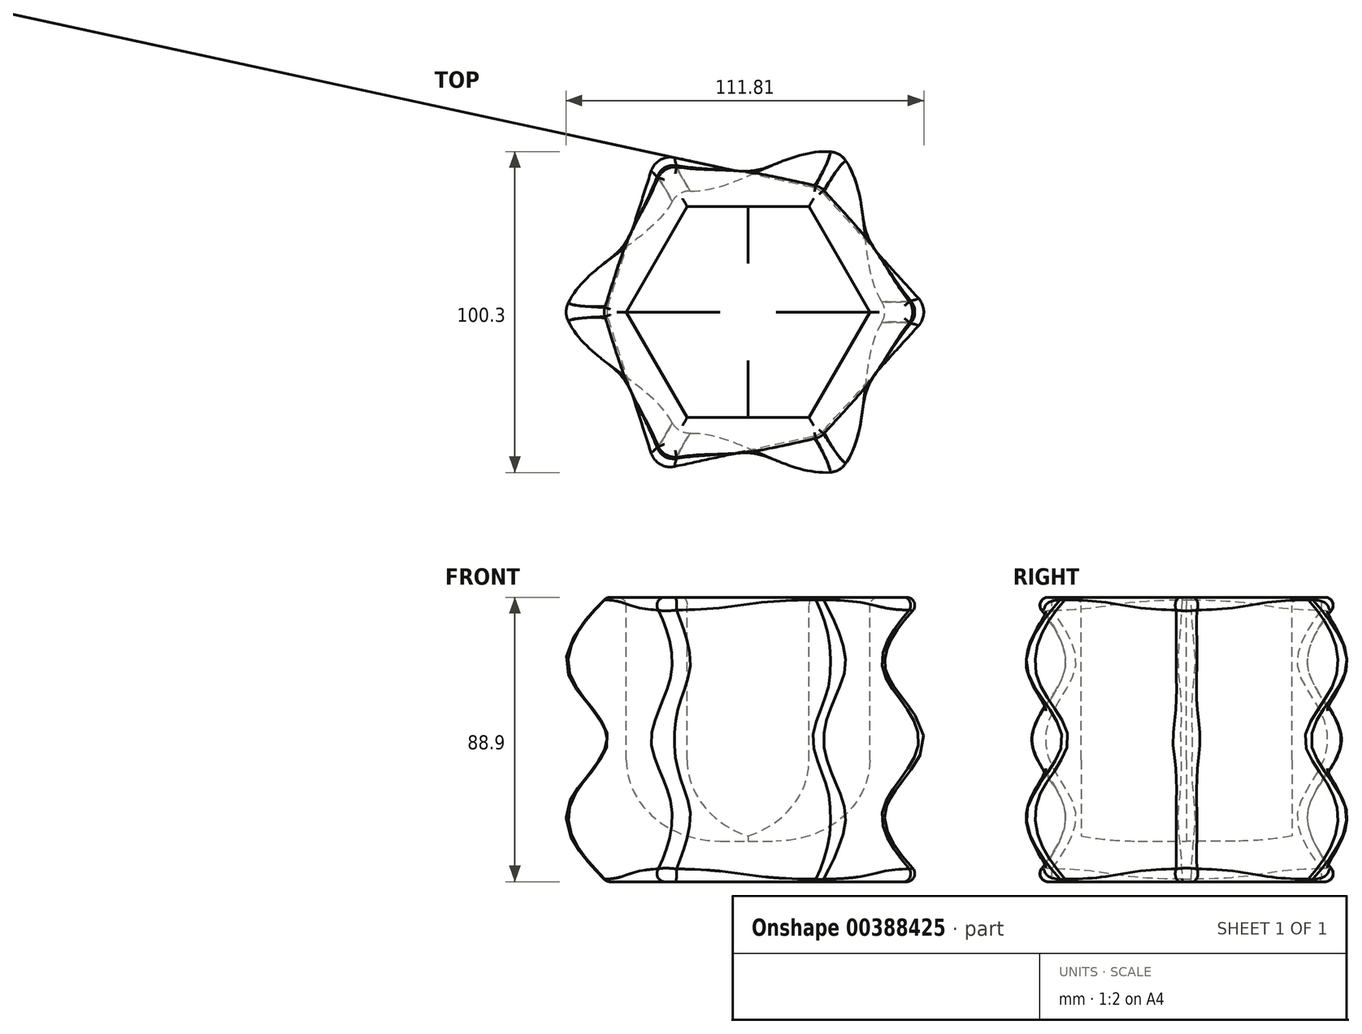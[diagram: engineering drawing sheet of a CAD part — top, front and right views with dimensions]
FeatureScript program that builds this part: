
annotation { "Feature Type Name" : "Feature", "Feature Type Description" : "" }
export const myFeature = defineFeature(function(context is Context, id is Id, definition is map)
    precondition{}
    {
        {
            var Q0;
            Q0=qCreatedBy(makeId("Top.planeOp"),FACE);
            var sketch = newSketch(context, id + "F0", { "sketchPlane" : qUnion([Q0])});
            skLineSegment(sketch, "E0.0", {"start": v(57.15, 0) * mm, "end": v(22.23, -38.5) * mm});
            skLineSegment(sketch, "E0.1", {"start": v(22.23, -38.5) * mm, "end": v(-28.58, -49.5) * mm});
            skLineSegment(sketch, "E0.2", {"start": v(-28.58, -49.5) * mm, "end": v(-44.45, 0) * mm});
            skLineSegment(sketch, "E0.3", {"start": v(-44.45, 0) * mm, "end": v(-28.58, 49.5) * mm});
            skLineSegment(sketch, "E0.4", {"start": v(-28.58, 49.5) * mm, "end": v(22.22, 38.5) * mm});
            skLineSegment(sketch, "E0.5", {"start": v(22.22, 38.5) * mm, "end": v(57.15, 0) * mm});
            skLineSegment(sketch, "E1", {"start": v(0, 0) * mm, "end": v(22.22, 38.5) * mm, "construction": true});
            skLineSegment(sketch, "E2", {"start": v(0, 0) * mm, "end": v(57.15, 0) * mm, "construction": true});
            skLineSegment(sketch, "E3", {"start": v(0, 0) * mm, "end": v(22.23, -38.5) * mm, "construction": true});
            skLineSegment(sketch, "E4", {"start": v(0, 0) * mm, "end": v(-28.58, -49.5) * mm, "construction": true});
            skLineSegment(sketch, "E5", {"start": v(0, 0) * mm, "end": v(-44.45, 0) * mm, "construction": true});
            skLineSegment(sketch, "E6", {"start": v(0, 0) * mm, "end": v(-28.58, 49.5) * mm, "construction": true});
            skSolve(sketch);
        }
        {
            var Q0;
            Q0=qCreatedBy(makeId("Top.planeOp"),FACE);
            cPlane(context, id + "F1", {"entities" : qUnion([Q0]), "cplaneType" : CPlaneType.OFFSET, "offset" : 88.9 * mm, "width" : 152.4 * mm, "height" : 152.4 * mm});
        }
        {
            var Q0;
            Q0=qCreatedBy(id+"F1.planeOp",FACE);
            var sketch = newSketch(context, id + "F2", { "sketchPlane" : qUnion([Q0])});
            skLineSegment(sketch, "E7.0.0", {"start": v(57.15, 0) * mm, "end": v(22.22, 38.5) * mm});
            skLineSegment(sketch, "E7.0.1", {"start": v(22.22, 38.5) * mm, "end": v(-28.58, 49.5) * mm});
            skLineSegment(sketch, "E7.0.2", {"start": v(-28.58, 49.5) * mm, "end": v(-44.45, 0) * mm});
            skLineSegment(sketch, "E7.0.3", {"start": v(-44.45, 0) * mm, "end": v(-28.58, -49.5) * mm});
            skLineSegment(sketch, "E7.0.4", {"start": v(-28.58, -49.5) * mm, "end": v(22.23, -38.5) * mm});
            skLineSegment(sketch, "E7.0.5", {"start": v(22.23, -38.5) * mm, "end": v(57.15, 0) * mm});
            skSolve(sketch);
        }
        {
            var Q0;
            Q0=sQuery(id+"F2.wireOp",VERTEX,"E7.0.3.start");
            var Q1;
            Q1=sQuery(id+"F2.wireOp",VERTEX,"E7.0.0.start");
            var Q2;
            Q2=sQuery(id+"F0.wireOp",VERTEX,"E0.5.end");
            cPlane(context, id + "F3", {"entities" : qUnion([Q0, Q1, Q2]), "cplaneType" : CPlaneType.THREE_POINT, "offset" : 25.4 * mm, "width" : 152.4 * mm, "height" : 152.4 * mm});
        }
        {
            var Q0;
            Q0=sQuery(id+"F2.wireOp",VERTEX,"E7.0.1.end");
            var Q1;
            Q1=sQuery(id+"F2.wireOp",VERTEX,"E7.0.5.start");
            var Q2;
            Q2=sQuery(id+"F0.wireOp",VERTEX,"E0.0.end");
            cPlane(context, id + "F4", {"entities" : qUnion([Q0, Q1, Q2]), "cplaneType" : CPlaneType.THREE_POINT, "offset" : 25.4 * mm, "width" : 152.4 * mm, "height" : 152.4 * mm});
        }
        {
            var Q0;
            Q0=sQuery(id+"F2.wireOp",VERTEX,"E7.0.1.start");
            var Q1;
            Q1=sQuery(id+"F2.wireOp",VERTEX,"E7.0.4.start");
            var Q2;
            Q2=sQuery(id+"F0.wireOp",VERTEX,"E0.2.start");
            cPlane(context, id + "F5", {"entities" : qUnion([Q0, Q1, Q2]), "cplaneType" : CPlaneType.THREE_POINT, "offset" : 25.4 * mm, "width" : 152.4 * mm, "height" : 152.4 * mm});
        }
        {
            var Q0;
            Q0=qCreatedBy(id+"F3.planeOp",FACE);
            var sketch = newSketch(context, id + "F6", { "sketchPlane" : qUnion([Q0])});
            skFitSpline(sketch, "E8", {"points": [v(-44.45, 0) * mm, v(-57.15, 22.23) * mm, v(-44.45, 44.45) * mm, v(-57.15, 66.67) * mm, v(-44.45, 88.9) * mm], "startDerivative": vector(-76.2, 76.2) * mm, "endDerivative": vector(76.2, 76.2) * mm});
            skFitSpline(sketch, "E9", {"points": [v(57.15, 0) * mm, v(44.45, 22.22) * mm, v(57.15, 44.45) * mm, v(44.45, 66.68) * mm, v(57.15, 88.9) * mm], "startDerivative": vector(-76.2, 76.2) * mm, "endDerivative": vector(76.2, 76.2) * mm});
            skSolve(sketch);
        }
        {
            var Q0;
            Q0=qCreatedBy(id+"F4.planeOp",FACE);
            var sketch = newSketch(context, id + "F7", { "sketchPlane" : qUnion([Q0])});
            skFitSpline(sketch, "E10", {"points": [v(-57.15, 88.9) * mm, v(-44.45, 66.68) * mm, v(-57.15, 44.45) * mm, v(-44.45, 22.23) * mm, v(-57.15, 0) * mm], "startDerivative": vector(76.2, -76.2) * mm, "endDerivative": vector(-76.2, -76.2) * mm});
            skFitSpline(sketch, "E11", {"points": [v(44.45, 88.9) * mm, v(57.15, 66.68) * mm, v(44.45, 44.45) * mm, v(57.15, 22.23) * mm, v(44.45, 0) * mm], "startDerivative": vector(76.2, -76.2) * mm, "endDerivative": vector(-76.2, -76.2) * mm});
            skSolve(sketch);
        }
        {
            var Q0;
            Q0=qCreatedBy(id+"F5.planeOp",FACE);
            var sketch = newSketch(context, id + "F8", { "sketchPlane" : qUnion([Q0])});
            skFitSpline(sketch, "E12", {"points": [v(-44.45, 0) * mm, v(-57.15, 22.23) * mm, v(-44.45, 44.45) * mm, v(-57.15, 66.68) * mm, v(-44.45, 88.9) * mm], "startDerivative": vector(-76.2, 76.2) * mm, "endDerivative": vector(76.2, 76.2) * mm});
            skFitSpline(sketch, "E13", {"points": [v(57.15, 0) * mm, v(44.45, 22.23) * mm, v(57.15, 44.45) * mm, v(44.45, 66.68) * mm, v(57.15, 88.9) * mm], "startDerivative": vector(-76.2, 76.2) * mm, "endDerivative": vector(76.2, 76.2) * mm});
            skSolve(sketch);
        }
        {
            var Q0;
            Q0=makeQuery(id+"F0.imprint","IMPRINT",FACE,{"disambiguationData":[TD([[makeQuery(id+"F0.imprint","IMPRINT",EDGE,{"derivedFrom":sQuery(id+"F0.wireOp",EDGE,"E0.0")}),-1.0]])]});
            var Q1;
            Q1=makeQuery(id+"F2.imprint","IMPRINT",FACE,{"disambiguationData":[TD([[makeQuery(id+"F2.imprint","IMPRINT",EDGE,{"derivedFrom":sQuery(id+"F2.wireOp",EDGE,"E7.0.0")}),1.0]])]});
            var Q2;
            Q2=sQuery(id+"F8.wireOp",EDGE,"E12");
            var Q3;
            Q3=sQuery(id+"F7.wireOp",EDGE,"E10");
            var Q4;
            Q4=sQuery(id+"F6.wireOp",EDGE,"E8");
            var Q5;
            Q5=sQuery(id+"F8.wireOp",EDGE,"E13");
            var Q6;
            Q6=sQuery(id+"F7.wireOp",EDGE,"E11");
            var Q7;
            Q7=sQuery(id+"F6.wireOp",EDGE,"E9");
            loft(context, id + "F9", {"addGuides" : true, "sheetProfilesArray" : [{ "sheetProfileEntities" : qUnion([Q0]) }, { "sheetProfileEntities" : qUnion([Q1]) }], "guidesArray" : [{ "guideEntities" : qUnion([Q2]), "guideDerivativeType" : LoftGuideDerivativeType.DEFAULT, "guideDerivativeMagnitude" : 1 }, { "guideEntities" : qUnion([Q3]), "guideDerivativeType" : LoftGuideDerivativeType.DEFAULT, "guideDerivativeMagnitude" : 1 }, { "guideEntities" : qUnion([Q4]), "guideDerivativeType" : LoftGuideDerivativeType.DEFAULT, "guideDerivativeMagnitude" : 1 }, { "guideEntities" : qUnion([Q5]), "guideDerivativeType" : LoftGuideDerivativeType.DEFAULT, "guideDerivativeMagnitude" : 1 }, { "guideEntities" : qUnion([Q6]), "guideDerivativeType" : LoftGuideDerivativeType.DEFAULT, "guideDerivativeMagnitude" : 1 }, { "guideEntities" : qUnion([Q7]), "guideDerivativeType" : LoftGuideDerivativeType.DEFAULT, "guideDerivativeMagnitude" : 1 }]});
        }
        {
            var Q0;
            Q0=makeQuery(id+"F9.opLoft","SWEPT_EDGE",EDGE,{"disambiguationData":[OSD([sQuery(id+"F7.wireOp",EDGE,"E10")])]});
            var Q1;
            Q1=makeQuery(id+"F9.opLoft","SWEPT_EDGE",EDGE,{"disambiguationData":[OSD([sQuery(id+"F6.wireOp",EDGE,"E8")])]});
            var Q2;
            Q2=makeQuery(id+"F9.opLoft","SWEPT_EDGE",EDGE,{"disambiguationData":[OSD([sQuery(id+"F8.wireOp",EDGE,"E13")])]});
            var Q3;
            Q3=makeQuery(id+"F9.opLoft","SWEPT_EDGE",EDGE,{"disambiguationData":[OSD([sQuery(id+"F7.wireOp",EDGE,"E11")])]});
            var Q4;
            Q4=makeQuery(id+"F9.opLoft","SWEPT_EDGE",EDGE,{"disambiguationData":[OSD([sQuery(id+"F6.wireOp",EDGE,"E9")])]});
            var Q5;
            Q5=makeQuery(id+"F9.opLoft","SWEPT_EDGE",EDGE,{"disambiguationData":[OSD([sQuery(id+"F8.wireOp",EDGE,"E12")])]});
            fillet(context, id + "F10", {"entities" : qUnion([Q0, Q1, Q2, Q3, Q4, Q5]), "radius" : 6.35 * mm, "tangentPropagation" : true, "allowEdgeOverflow" : false});
        }
        {
            var Q0;
            Q0=makeQuery(id+"F9.opLoft","CAP_FACE",FACE,{"disambiguationData":[OSD([makeQuery(id+"F2.imprint","IMPRINT",FACE,{"disambiguationData":[TD([[makeQuery(id+"F2.imprint","IMPRINT",EDGE,{"derivedFrom":sQuery(id+"F2.wireOp",EDGE,"E7.0.0")}),1.0]])]})])],"isStart":true});
            var sketch = newSketch(context, id + "F11", { "sketchPlane" : qUnion([Q0])});
            skCircle(sketch, "E14.cCircle", {"center": v(0, 0) * mm, "radius": 38.1 * mm, "construction": true});
            skLineSegment(sketch, "E14.0", {"start": v(38.1, 0) * mm, "end": v(19.05, -33) * mm});
            skLineSegment(sketch, "E14.1", {"start": v(19.05, -33) * mm, "end": v(-19.05, -33) * mm});
            skLineSegment(sketch, "E14.2", {"start": v(-19.05, -33) * mm, "end": v(-38.1, 0) * mm});
            skLineSegment(sketch, "E14.3", {"start": v(-38.1, 0) * mm, "end": v(-19.05, 33) * mm});
            skLineSegment(sketch, "E14.4", {"start": v(-19.05, 33) * mm, "end": v(19.05, 33) * mm});
            skLineSegment(sketch, "E14.5", {"start": v(19.05, 33) * mm, "end": v(38.1, 0) * mm});
            skSolve(sketch);
        }
        {
            var Q0;
            Q0=makeQuery(id+"F11.imprint","IMPRINT",FACE,{"disambiguationData":[TD([[makeQuery(id+"F11.imprint","IMPRINT",EDGE,{"derivedFrom":sQuery(id+"F11.wireOp",EDGE,"E14.0")}),-1.0]])]});
            extrude(context, id + "F12", {"entities" : qUnion([Q0]), "operationType" : NewBodyOperationType.REMOVE, "oppositeDirection" : true, "depth" : 76.2 * mm});
        }
        {
            var Q0;
            Q0=makeQuery(id+"F9.opLoft","CAP_FACE",FACE,{"disambiguationData":[OSD([makeQuery(id+"F2.imprint","IMPRINT",FACE,{"disambiguationData":[TD([[makeQuery(id+"F2.imprint","IMPRINT",EDGE,{"derivedFrom":sQuery(id+"F2.wireOp",EDGE,"E7.0.0")}),1.0]])]})])],"isStart":true});
            var Q1;
            Q1=makeQuery(id+"F9.opLoft","CAP_FACE",FACE,{"disambiguationData":[OSD([makeQuery(id+"F0.imprint","IMPRINT",FACE,{"disambiguationData":[TD([[makeQuery(id+"F0.imprint","IMPRINT",EDGE,{"derivedFrom":sQuery(id+"F0.wireOp",EDGE,"E0.0")}),-1.0]])]})])],"isStart":true});
            fillet(context, id + "F13", {"entities" : qUnion([Q0, Q1]), "radius" : 2.54 * mm, "tangentPropagation" : true, "allowEdgeOverflow" : false});
        }
        {
            var Q0;
            Q0=makeQuery(id+"F12.boolean.opBoolean","COPY",EDGE,{"derivedFrom":makeQuery(id+"F12.opExtrude","CAP_EDGE",EDGE,{"disambiguationData":[OSD([sQuery(id+"F11.wireOp",EDGE,"E14.5")])],"isStart":false})});
            var Q1;
            Q1=makeQuery(id+"F12.boolean.opBoolean","COPY",EDGE,{"derivedFrom":makeQuery(id+"F12.opExtrude","CAP_EDGE",EDGE,{"disambiguationData":[OSD([sQuery(id+"F11.wireOp",EDGE,"E14.0")])],"isStart":false})});
            var Q2;
            Q2=makeQuery(id+"F12.boolean.opBoolean","COPY",EDGE,{"derivedFrom":makeQuery(id+"F12.opExtrude","CAP_EDGE",EDGE,{"disambiguationData":[OSD([sQuery(id+"F11.wireOp",EDGE,"E14.2")])],"isStart":false})});
            var Q3;
            Q3=makeQuery(id+"F12.boolean.opBoolean","COPY",EDGE,{"derivedFrom":makeQuery(id+"F12.opExtrude","CAP_EDGE",EDGE,{"disambiguationData":[OSD([sQuery(id+"F11.wireOp",EDGE,"E14.3")])],"isStart":false})});
            fillet(context, id + "F14", {"entities" : qUnion([Q0, Q1, Q2, Q3]), "radius" : 25.4 * mm, "tangentPropagation" : true, "allowEdgeOverflow" : false});
        }
    });
